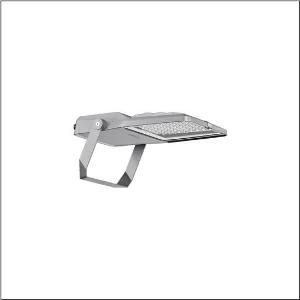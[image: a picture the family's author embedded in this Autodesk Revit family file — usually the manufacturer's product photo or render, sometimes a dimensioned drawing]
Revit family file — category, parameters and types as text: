
# Revit family: floodlight_fl_21_iq_mini___pl43_5xa7771c2a1a_27d2
name_source: partatom
category: Lighting Fixtures
units: mm (PartAtom-declared; Revit-internal decimal feet)

## family parameters
Cut with Voids When Loaded = No
Host = Face
Light Source = No
Part Type = Normal
Room Calculation Point = No
Round Connector Dimension = Use Diameter
Shared = No

## types (1)
- --- (1 x LED, 12520 lm, 87.2 W, 3000K)
    Apparent Load = 87 VA
    CIE Flux Codes = 27 78 99 100 100
    Color Rendering = 70
    Color Temperature = 3000K
    Default Elevation = 1800 mm
    Description = Floodlight FL 21 iQ mini, floodlight, primary light control with lens, of PMMA, primary optical cover: protective disc, of toughened safety glass, transparent, light distribution: PL43, light emission: direct distribution, installation type: surface-mounted, lamps: LED, High Power LED, rated values: 12.520lm | 87,2W | 143,6lm/W (begin service life); end service life: 12.520lm | 92,1W; at 50% lumin. flux: 6.260lm | 40,1W | 156,1lm/W, colour temperature: 3000K, colour rendering: CRI > 70, light colour: 730, light setting 1 begin service life: 100% | 12.520lm | 87,2W | 143,6lm/W | 3.000K, light setting 1 end service life: 92,1W, further light settings possible, control: Auto-Match, Temp-Guard, Lumen-Switch, Night-Set, Smart-Wire, Light-Fading, Desk-Remote (wireless, voltage-free reading and setting of iQ features in the workshop via application-optimized NFC function/RFID function), optimised constant luminous flux control (CLO 2.0), pre-setting: linear dimming characteristic, with terminal, 6-pole, mains connection: 220..240V, AC, 50/60Hz, luminaire housing, of diecast aluminium, powder-coated, SITECO metallic grey (DB 702S), corrosivity category C5 mid according to DIN EN ISO 12944suitable for swimming poolschlorine-resistant, sealing non-destructively replaceable, mounting bracket, of steel, galvanised, powder-coated, SITECO metallic grey (DB 702S), protection rating (complete): IP66, insulation class (complete): insulation class II (safety insulation), certification: CE, ENEC, VDE, protection symbol: D, impact resistance: IK08, permissible operating ambient temperature: -40..+40°C, permissible operating ambient temperature for outdoor applications: -40..+50°C, standard: DIN EN 12944, LABS conformity tested according to VDMA 24364:2018-05, packaging unit: 1 piece

Light Distribution: PL43
    Height = 70 mm
    Lamp = 1 x LED
    Lamp Light Flux = 12520 lm
    Lamp Power = 87.2 W
    Lamp count = 1
    Length = 485 mm
    Luminous efficacy = 144 lm/W
    Manufacturer = Siteco
    ModVariant = No
    Model = 5XA7771C2A1A
    Mounting Place = Pole
    Mounting Type = Pole annexe
    Number of Poles = 1
    OnlyDefault = Yes
    Power Factor = 1
    Product Name = Floodlight FL 21 iQ mini | PL43
    Product group = floodlight | pylon annexe
    ProductGroupID = 6201
    Protection Class = Protection class II
    Protection Degree = IP 66
    RLX_Detail_Level = 1
    RLX_Emergency_Light_Flux = 0 lm
    RLX_Emergency_Type = 0
    RLX_Emergency_Type_DB = No
    RlxData = <blob elided: 96489 chars, md5=13e223c6>
    Socket = socket
    Standby Power = 0 W
    System Light Flux = 12520 lm
    System Power = 87 W
    Type Comments = factory setting: luminous flux: 100 % | dim-lin: 254 | 456 mA
    Type Image = l_1006845.jpg
    URL = http://relux.com
    VarID = @adj_163627
    Voltage = 0 V
    Weight = 0.00 kg
    Width = 337 mm

## geometry (parser evidence)
native form markers: Blend x4, Sweep x11
no freeform markers — native parametric forms only
